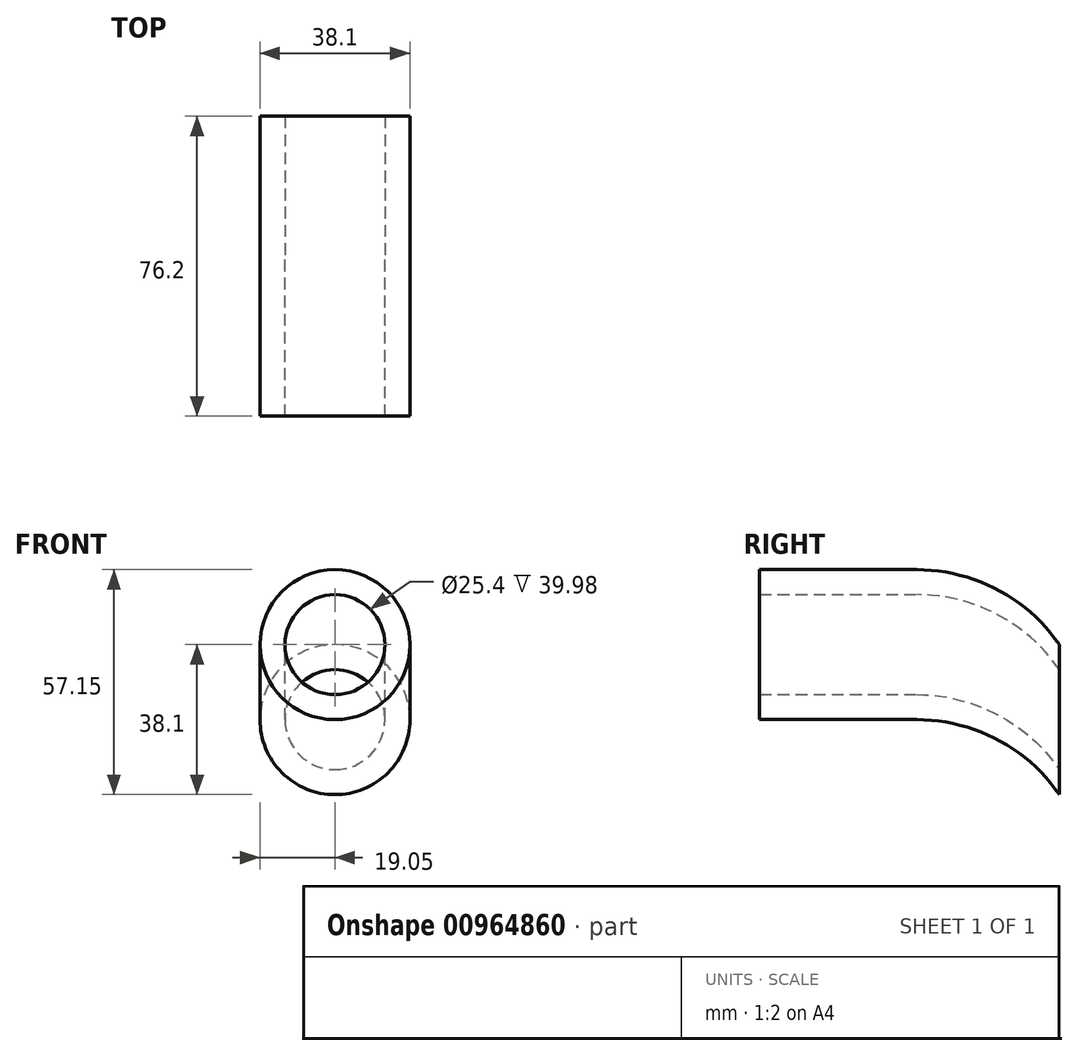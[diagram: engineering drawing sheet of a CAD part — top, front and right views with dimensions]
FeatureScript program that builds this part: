
annotation { "Feature Type Name" : "Feature", "Feature Type Description" : "" }
export const myFeature = defineFeature(function(context is Context, id is Id, definition is map)
    precondition{}
    {
        {
            var Q0;
            Q0=qCreatedBy(makeId("Front.planeOp"),FACE);
            var sketch = newSketch(context, id + "F0", { "sketchPlane" : qUnion([Q0])});
            skCircle(sketch, "E0", {"center": v(0, 0) * mm, "radius": 19.05 * mm});
            skCircle(sketch, "E1", {"center": v(0, 0) * mm, "radius": 12.7 * mm});
            skSolve(sketch);
        }
        {
            var Q0;
            Q0=qCreatedBy(makeId("Right.planeOp"),FACE);
            var sketch = newSketch(context, id + "F1", { "sketchPlane" : qUnion([Q0])});
            skLineSegment(sketch, "E2", {"start": v(0, 0) * mm, "end": v(39.98, 0) * mm});
            skArc(sketch, "E3", {"start": v(76.2, -19.05) * mm, "mid": v(60.44, -5.05) * mm, "end": v(39.98, 0) * mm});
            skSolve(sketch);
        }
        {
            var Q0;
            Q0=makeQuery(id+"F0.imprint","IMPRINT",FACE,{"disambiguationData":[TD([[makeQuery(id+"F0.imprint","IMPRINT",EDGE,{"derivedFrom":sQuery(id+"F0.wireOp",EDGE,"E0")}),1.0]])]});
            var Q1;
            Q1=sQuery(id+"F1.wireOp",EDGE,"E2");
            var Q2;
            Q2=sQuery(id+"F1.wireOp",EDGE,"E3");
            sweep(context, id + "F2", {"profiles" : qUnion([Q0]), "path" : qUnion([Q1, Q2]), "keepProfileOrientation" : true});
        }
    });
